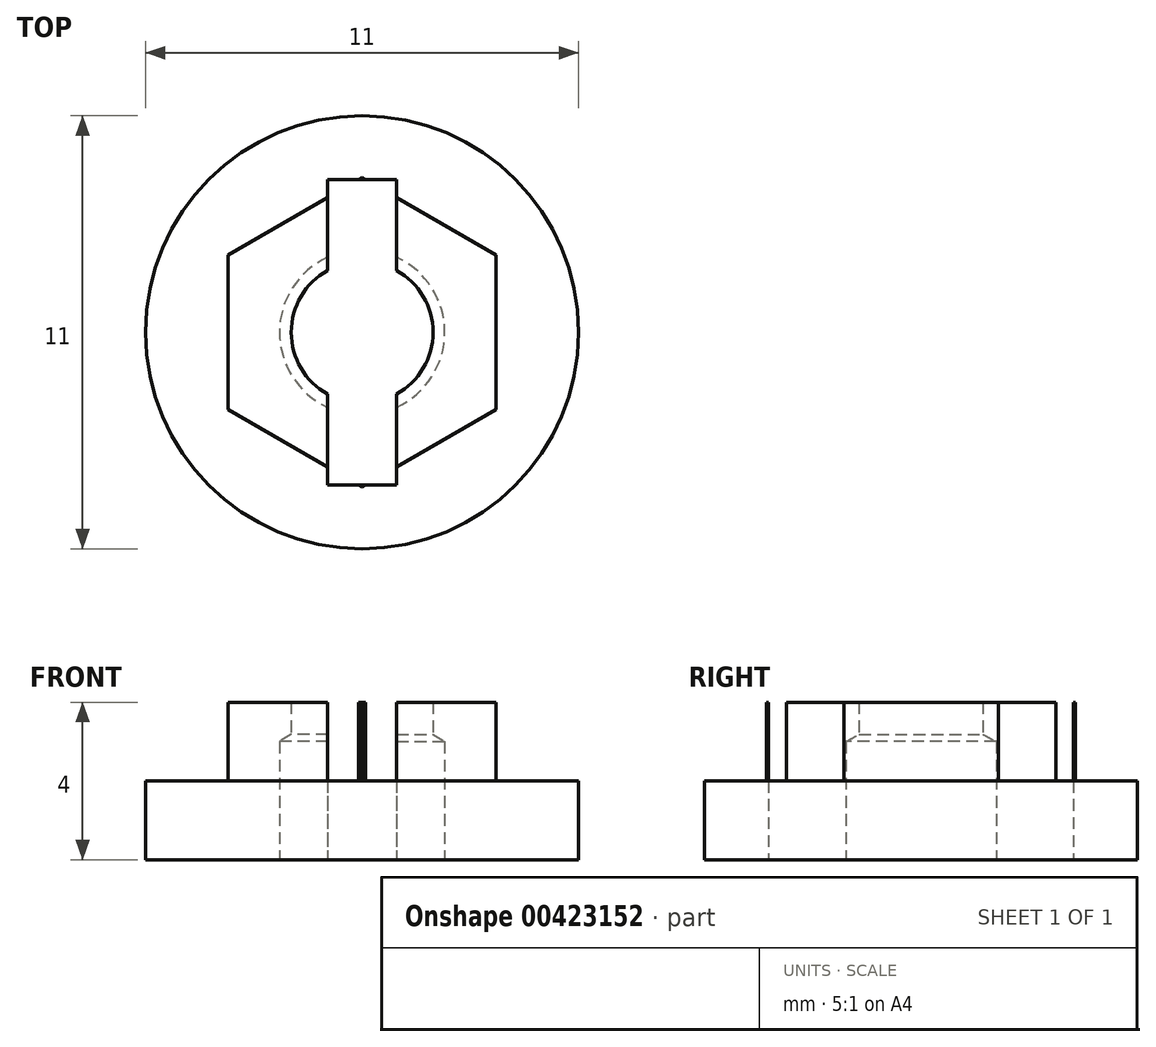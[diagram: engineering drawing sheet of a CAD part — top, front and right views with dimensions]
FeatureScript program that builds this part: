
annotation { "Feature Type Name" : "Feature", "Feature Type Description" : "" }
export const myFeature = defineFeature(function(context is Context, id is Id, definition is map)
    precondition{}
    {
        {
            assignVariable(context, id + "F0", {"name" : "hex_height", "anyValue" : 4});
        }
        {
            assignVariable(context, id + "F1", {"name" : "shaft_hole_diameter", "anyValue" : 3.6});
        }
        {
            assignVariable(context, id + "F2", {"name" : "base_hole_diameter", "anyValue" : 4.2});
        }
        {
            assignVariable(context, id + "F3", {"name" : "base_hole_depth", "anyValue" : 3});
        }
        {
            var Q0;
            Q0=qCreatedBy(makeId("Top.planeOp"),FACE);
            var sketch = newSketch(context, id + "F4", { "sketchPlane" : qUnion([Q0])});
            skPoint(sketch, "E0", {"position": v(0, 0) * mm});
            skCircle(sketch, "E1.cCircle", {"center": v(0, 0) * mm, "radius": 3.4 * mm, "construction": true});
            skLineSegment(sketch, "E1.0", {"start": v(3.4, 1.96) * mm, "end": v(3.4, -1.96) * mm});
            skLineSegment(sketch, "E1.1", {"start": v(3.4, -1.96) * mm, "end": v(0, -3.93) * mm});
            skLineSegment(sketch, "E1.2", {"start": v(0, -3.93) * mm, "end": v(-3.4, -1.96) * mm});
            skLineSegment(sketch, "E1.3", {"start": v(-3.4, -1.96) * mm, "end": v(-3.4, 1.96) * mm});
            skLineSegment(sketch, "E1.4", {"start": v(-3.4, 1.96) * mm, "end": v(0, 3.93) * mm});
            skLineSegment(sketch, "E1.5", {"start": v(0, 3.93) * mm, "end": v(3.4, 1.96) * mm});
            skPoint(sketch, "E1.0.midPoint", {"position": v(3.4, 0) * mm});
            skCircle(sketch, "E2", {"center": v(0, 0) * mm, "radius": 5.5 * mm});
            skSolve(sketch);
        }
        {
            var Q0;
            {var subQ0=sQuery(id+"F4.wireOp",EDGE,"E1.0");Q0=makeQuery(id+"F4.imprint","IMPRINT",FACE,{"disambiguationData":[TD([[makeQuery(id+"F4.imprint","IMPRINT",EDGE,{"derivedFrom":subQ0}),-1.0]])]});}
            var Q1;
            {var subQ0=sQuery(id+"F4.wireOp",EDGE,"E1.3");Q1=makeQuery(id+"F4.imprint","IMPRINT",FACE,{"disambiguationData":[TD([[makeQuery(id+"F4.imprint","IMPRINT",EDGE,{"derivedFrom":subQ0}),-1.0]])]});}
            var Q2;
            {var subQ5=sQuery(id+"F4.wireOp",EDGE,"E1.2");var subQ6=sQuery(id+"F4.wireOp",EDGE,"E1.1");var subQ7=makeQuery(id+"F4.imprint","INTERSECT",VERTEX,{"derivedFrom":[subQ6,subQ5]});Q2=makeQuery(id+"F4.imprint","IMPRINT",FACE,{"disambiguationData":[TD([[makeQuery(id+"F4.imprint","IMPRINT",EDGE,{"disambiguationData":[TD([[subQ7,1.0]])],"derivedFrom":subQ6}),-1.0]])]});}
            extrude(context, id + "F5", {"entities" : qUnion([Q0, Q1, Q2]), "depth" : (getVariable(context, 'hex_height')) * mm});
        }
        {
            var Q0;
            Q0 = qSketchRegion(id + "F4", true);
            extrude(context, id + "F6", {"entities" : qUnion([Q0]), "operationType" : NewBodyOperationType.ADD, "depth" : 2 * mm});
        }
        {
            var Q0;
            Q0=qCreatedBy(makeId("Top.planeOp"),FACE);
            var sketch = newSketch(context, id + "F7", { "sketchPlane" : qUnion([Q0])});
            skPoint(sketch, "E3.middle", {"position": v(0, 0) * mm});
            skLineSegment(sketch, "E4.bottom", {"start": v(0.88, 3.88) * mm, "end": v(-0.87, 3.88) * mm});
            skLineSegment(sketch, "E4.top", {"start": v(0.88, -3.88) * mm, "end": v(-0.88, -3.88) * mm});
            skLineSegment(sketch, "E4.left", {"start": v(0.88, 3.88) * mm, "end": v(0.88, -3.88) * mm});
            skLineSegment(sketch, "E4.right", {"start": v(-0.87, 3.88) * mm, "end": v(-0.88, -3.88) * mm});
            skSolve(sketch);
        }
        {
            var Q0;
            Q0 = qSketchRegion(id + "F7", true);
            var Q1;
            Q1=makeQuery(id+"F5.opExtrude","CAP_FACE",FACE,{"disambiguationData":[OSD([sQuery(id+"F4.wireOp",EDGE,"E1.0"),sQuery(id+"F4.wireOp",EDGE,"E1.1"),sQuery(id+"F4.wireOp",EDGE,"E1.2"),sQuery(id+"F4.wireOp",EDGE,"E1.3"),sQuery(id+"F4.wireOp",EDGE,"E1.4"),sQuery(id+"F4.wireOp",EDGE,"E1.5")])],"isStart":false});
            extrude(context, id + "F8", {"entities" : qUnion([Q0]), "operationType" : NewBodyOperationType.REMOVE, "oppositeDirection" : true, "endBoundEntityFace" : qUnion([Q1]), "depth" : -5 * mm});
        }
        {
            var Q0;
            {var subQ0=sQuery(id+"F4.wireOp",EDGE,"E1.5");var subQ1=sQuery(id+"F4.wireOp",EDGE,"E1.4");var subQ2=sQuery(id+"F4.wireOp",EDGE,"E1.3");var subQ3=sQuery(id+"F4.wireOp",EDGE,"E1.2");var subQ4=sQuery(id+"F4.wireOp",EDGE,"E1.1");var subQ5=sQuery(id+"F4.wireOp",EDGE,"E1.0");Q0=makeQuery(id+"F6.boolean.opBoolean","MERGE",FACE,{"derivedFrom":[makeQuery(id+"F5.opExtrude","CAP_FACE",FACE,{"disambiguationData":[OSD([subQ5,subQ4,subQ3,subQ2,subQ1,subQ0])],"isStart":true}),makeQuery(id+"F6.opExtrude","CAP_FACE",FACE,{"disambiguationData":[OSD([subQ5,subQ4,subQ3,subQ2,subQ1,subQ0,sQuery(id+"F4.wireOp",EDGE,"E2"),sQuery(id+"F4.wireOp",EDGE,"XI2Bt1tW-WjUK-xKQc-PAp0-KQXT2wfpSORE.bottom"),sQuery(id+"F4.wireOp",EDGE,"XI2Bt1tW-WjUK-xKQc-PAp0-KQXT2wfpSORE.top"),sQuery(id+"F4.wireOp",EDGE,"XI2Bt1tW-WjUK-xKQc-PAp0-KQXT2wfpSORE.left"),sQuery(id+"F4.wireOp",EDGE,"XI2Bt1tW-WjUK-xKQc-PAp0-KQXT2wfpSORE.right")])],"isStart":true})]});}
            var sketch = newSketch(context, id + "F9", { "sketchPlane" : qUnion([Q0])});
            skPoint(sketch, "E5", {"position": v(0, 0) * mm});
            skSolve(sketch);
        }
        {
            var Q0;
            Q0=sQuery(id+"F9.wireOp",VERTEX,"E5");
            var Q1;
            Q1=makeQuery(id+"F5.opExtrude","SWEPT_BODY",BODY,{"disambiguationData":[OSD([sQuery(id+"F4.wireOp",EDGE,"E1.0"),sQuery(id+"F4.wireOp",EDGE,"E1.1"),sQuery(id+"F4.wireOp",EDGE,"E1.2"),sQuery(id+"F4.wireOp",EDGE,"E1.3"),sQuery(id+"F4.wireOp",EDGE,"E1.4"),sQuery(id+"F4.wireOp",EDGE,"E1.5")])]});
            hole(context, id + "F10", {"style" : HoleStyle.SIMPLE, "endStyle" : HoleEndStyle.THROUGH, "holeDiameter" : (getVariable(context, 'shaft_hole_diameter')) * mm, "isTappedThrough" : true, "tappedDepth" : 12.7 * mm, "tapClearance" : 3, "locations" : qUnion([Q0]), "scope" : qUnion([Q1])});
        }
        {
            var Q0;
            Q0=sQuery(id+"F9.wireOp",VERTEX,"E5");
            var Q1;
            Q1=makeQuery(id+"F5.opExtrude","SWEPT_BODY",BODY,{"disambiguationData":[OSD([sQuery(id+"F4.wireOp",EDGE,"E1.0"),sQuery(id+"F4.wireOp",EDGE,"E1.1"),sQuery(id+"F4.wireOp",EDGE,"E1.2"),sQuery(id+"F4.wireOp",EDGE,"E1.3"),sQuery(id+"F4.wireOp",EDGE,"E1.4"),sQuery(id+"F4.wireOp",EDGE,"E1.5")])]});
            hole(context, id + "F11", {"style" : HoleStyle.SIMPLE, "endStyle" : HoleEndStyle.BLIND, "holeDiameter" : (getVariable(context, 'base_hole_diameter')) * mm, "holeDepth" : (getVariable(context, 'base_hole_depth')) * mm, "isTappedThrough" : true, "tappedDepth" : 12.7 * mm, "tapClearance" : 3, "startFromSketch" : true, "locations" : qUnion([Q0]), "scope" : qUnion([Q1])});
        }
    });
